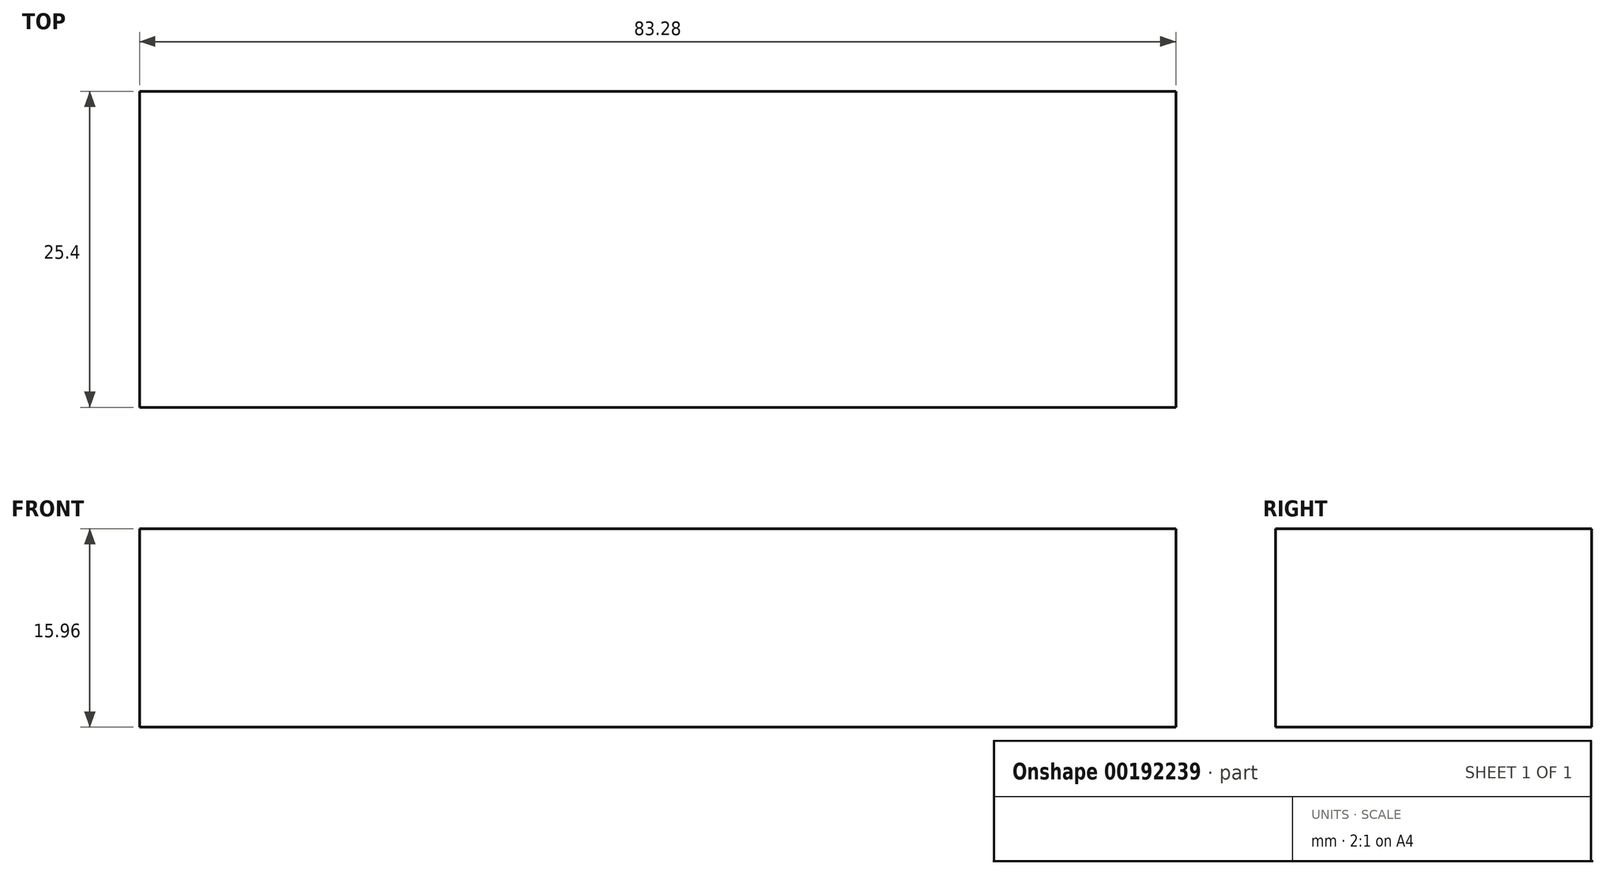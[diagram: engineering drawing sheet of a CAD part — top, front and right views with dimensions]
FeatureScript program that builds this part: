
annotation { "Feature Type Name" : "Feature", "Feature Type Description" : "" }
export const myFeature = defineFeature(function(context is Context, id is Id, definition is map)
    precondition{}
    {
        {
            var Q0;
            Q0=qCreatedBy(makeId("Front.planeOp"),FACE);
            var sketch = newSketch(context, id + "F0", { "sketchPlane" : qUnion([Q0])});
            skLineSegment(sketch, "E0.bottom", {"start": v(-133.91, 41.18) * mm, "end": v(-50.63, 41.18) * mm});
            skLineSegment(sketch, "E0.top", {"start": v(-133.91, 25.22) * mm, "end": v(-50.63, 25.22) * mm});
            skLineSegment(sketch, "E0.left", {"start": v(-133.91, 41.18) * mm, "end": v(-133.91, 25.22) * mm});
            skLineSegment(sketch, "E0.right", {"start": v(-50.63, 41.18) * mm, "end": v(-50.63, 25.22) * mm});
            skSolve(sketch);
        }
        {
            var Q0;
            Q0=makeQuery(id+"F0.imprint","IMPRINT",FACE,{"disambiguationData":[TD([[makeQuery(id+"F0.imprint","IMPRINT",EDGE,{"derivedFrom":sQuery(id+"F0.wireOp",EDGE,"E0.bottom")}),-1.0]])]});
            extrude(context, id + "F1", {"entities" : qUnion([Q0]), "depth" : 25.4 * mm});
        }
    });
